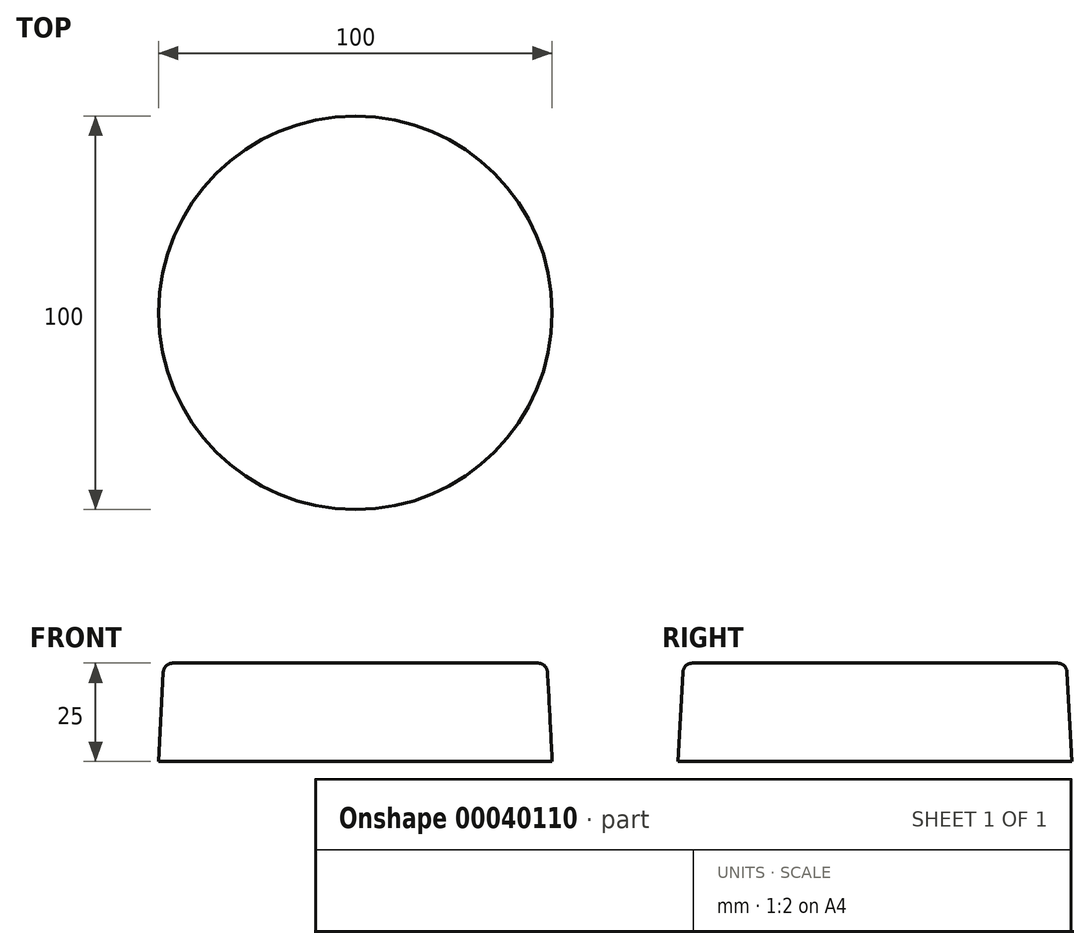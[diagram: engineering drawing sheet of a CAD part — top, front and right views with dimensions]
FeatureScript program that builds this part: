
annotation { "Feature Type Name" : "Feature", "Feature Type Description" : "" }
export const myFeature = defineFeature(function(context is Context, id is Id, definition is map)
    precondition{}
    {
        {
            var Q0;
            Q0=qCreatedBy(makeId("Top.planeOp"),FACE);
            var sketch = newSketch(context, id + "F0", { "sketchPlane" : qUnion([Q0])});
            skCircle(sketch, "E0", {"center": v(0, 0) * mm, "radius": 50 * mm});
            skSolve(sketch);
        }
        {
            var Q0;
            Q0 = qSketchRegion(id + "F0", true);
            extrude(context, id + "F1", {"entities" : qUnion([Q0]), "depth" : 25 * mm, "hasDraft" : true, "draftAngle" : 3 * degree, "draftPullDirection" : true});
        }
        {
            var Q0;
            Q0=makeQuery(id+"F1.opExtrude","CAP_FACE",FACE,{"disambiguationData":[OSD([sQuery(id+"F0.wireOp",EDGE,"E0")])],"isStart":false});
            fillet(context, id + "F2", {"entities" : qUnion([Q0]), "radius" : 2.5 * mm, "tangentPropagation" : true, "allowEdgeOverflow" : false});
        }
    });
